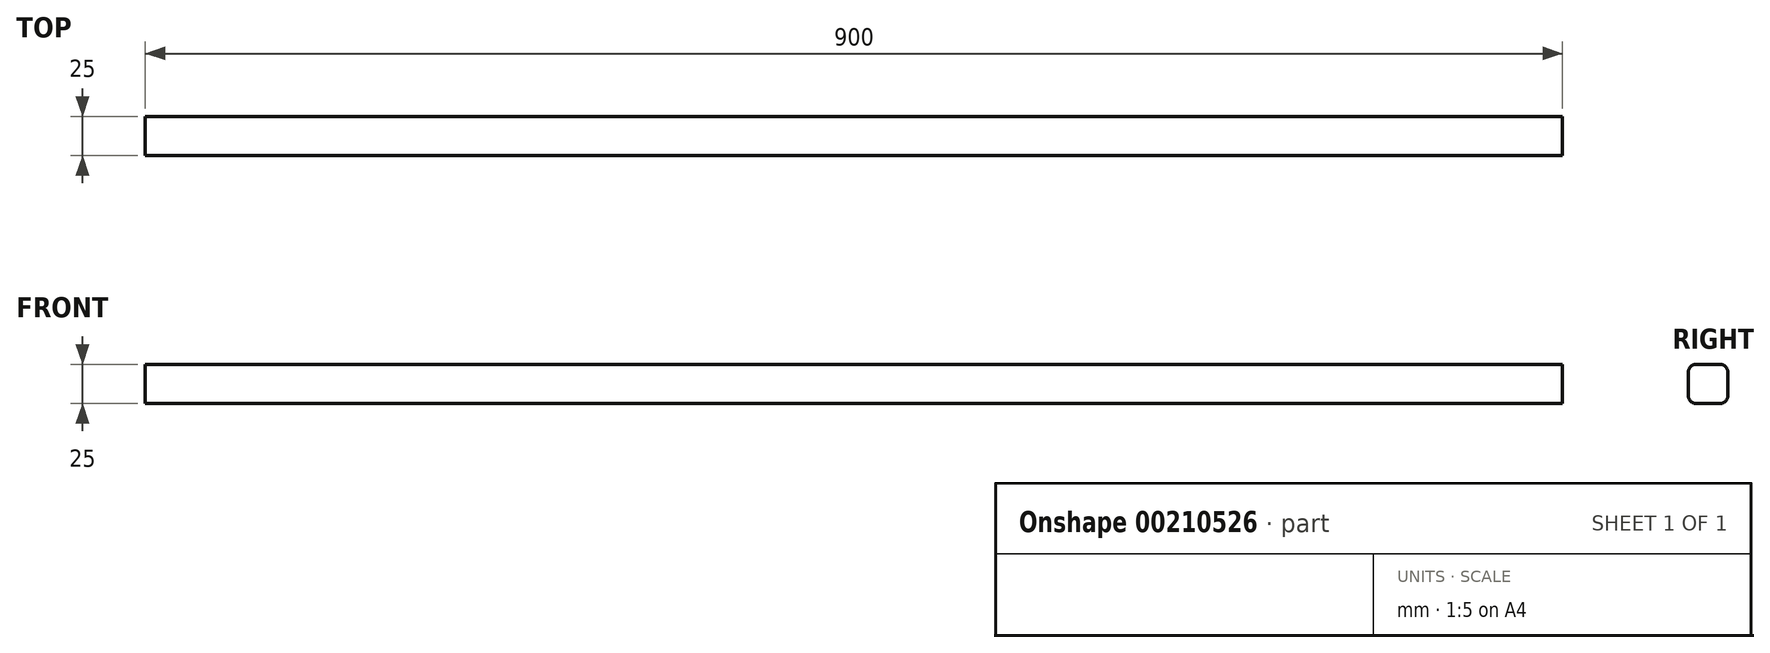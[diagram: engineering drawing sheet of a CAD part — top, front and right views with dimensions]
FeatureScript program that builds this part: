
annotation { "Feature Type Name" : "Feature", "Feature Type Description" : "" }
export const myFeature = defineFeature(function(context is Context, id is Id, definition is map)
    precondition{}
    {
        {
            var Q0;
            Q0=qCreatedBy(makeId("Top.planeOp"),FACE);
            var sketch = newSketch(context, id + "F0", { "sketchPlane" : qUnion([Q0])});
            skLineSegment(sketch, "E0.bottom", {"start": v(450, 12.5) * mm, "end": v(-450, 12.5) * mm});
            skLineSegment(sketch, "E0.top", {"start": v(450, -12.5) * mm, "end": v(-450, -12.5) * mm});
            skLineSegment(sketch, "E0.left", {"start": v(450, 12.5) * mm, "end": v(450, -12.5) * mm});
            skLineSegment(sketch, "E0.right", {"start": v(-450, 12.5) * mm, "end": v(-450, -12.5) * mm});
            skPoint(sketch, "E0.middle", {"position": v(0, 0) * mm});
            skSolve(sketch);
        }
        {
            var Q0;
            Q0=makeQuery(id+"F0.imprint","IMPRINT",FACE,{"disambiguationData":[TD([[makeQuery(id+"F0.imprint","IMPRINT",EDGE,{"derivedFrom":sQuery(id+"F0.wireOp",EDGE,"E0.bottom")}),1.0]])]});
            extrude(context, id + "F1", {"entities" : qUnion([Q0]), "depth" : 25 * mm});
        }
        {
            var Q0;
            Q0=makeQuery(id+"F1.opExtrude","CAP_EDGE",EDGE,{"disambiguationData":[OSD([sQuery(id+"F0.wireOp",EDGE,"E0.bottom")])],"isStart":false});
            fillet(context, id + "F2", {"entities" : qUnion([Q0]), "radius" : 5 * mm, "tangentPropagation" : true, "allowEdgeOverflow" : false});
        }
        {
            var Q0;
            Q0=makeQuery(id+"F1.opExtrude","CAP_EDGE",EDGE,{"disambiguationData":[OSD([sQuery(id+"F0.wireOp",EDGE,"E0.bottom")])],"isStart":true});
            fillet(context, id + "F3", {"entities" : qUnion([Q0]), "radius" : 5 * mm, "tangentPropagation" : true, "allowEdgeOverflow" : false});
        }
        {
            var Q0;
            Q0=makeQuery(id+"F1.opExtrude","CAP_EDGE",EDGE,{"disambiguationData":[OSD([sQuery(id+"F0.wireOp",EDGE,"E0.top")])],"isStart":true});
            fillet(context, id + "F4", {"entities" : qUnion([Q0]), "radius" : 5 * mm, "tangentPropagation" : true, "allowEdgeOverflow" : false});
        }
        {
            var Q0;
            Q0=makeQuery(id+"F1.opExtrude","CAP_EDGE",EDGE,{"disambiguationData":[OSD([sQuery(id+"F0.wireOp",EDGE,"E0.top")])],"isStart":false});
            fillet(context, id + "F5", {"entities" : qUnion([Q0]), "radius" : 5 * mm, "tangentPropagation" : true, "allowEdgeOverflow" : false});
        }
    });
